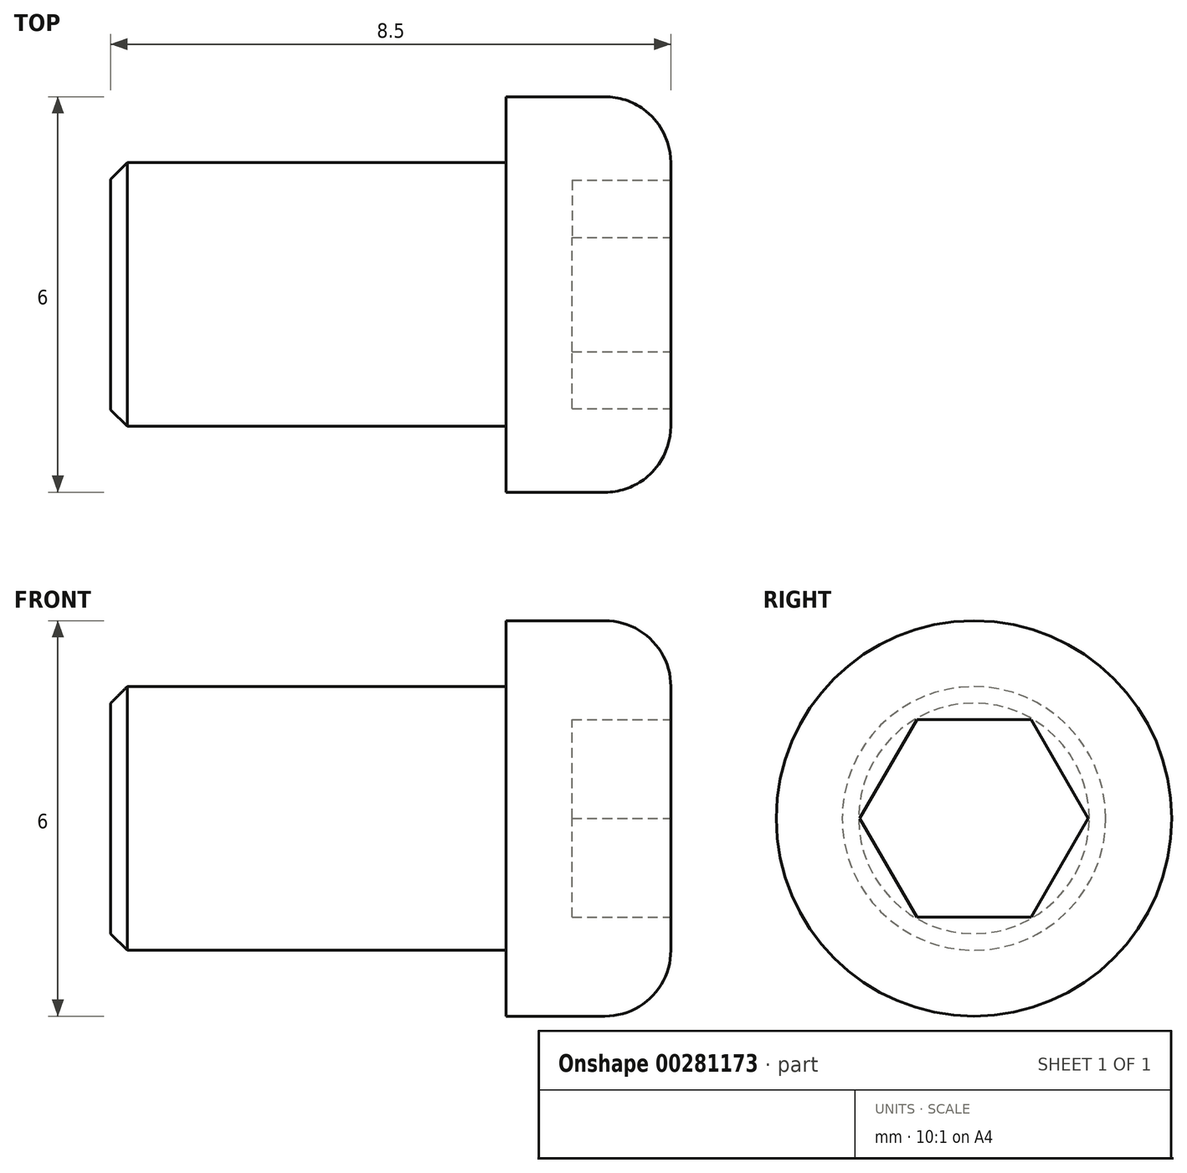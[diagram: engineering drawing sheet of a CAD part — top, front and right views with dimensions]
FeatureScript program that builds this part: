
annotation { "Feature Type Name" : "Feature", "Feature Type Description" : "" }
export const myFeature = defineFeature(function(context is Context, id is Id, definition is map)
    precondition{}
    {
        {
            var Q0;
            Q0=qCreatedBy(makeId("Front.planeOp"),FACE);
            var sketch = newSketch(context, id + "F0", { "sketchPlane" : qUnion([Q0])});
            skLineSegment(sketch, "E0", {"start": v(-4.25, 0) * mm, "end": v(-4.25, -2) * mm});
            skLineSegment(sketch, "E1", {"start": v(-4.25, -2) * mm, "end": v(1.75, -2) * mm});
            skLineSegment(sketch, "E2", {"start": v(1.75, -2) * mm, "end": v(1.75, -3) * mm});
            skLineSegment(sketch, "E3", {"start": v(1.75, -3) * mm, "end": v(4.25, -3) * mm});
            skLineSegment(sketch, "E4", {"start": v(4.25, -3) * mm, "end": v(4.25, 0) * mm});
            skLineSegment(sketch, "E5", {"start": v(4.25, 0) * mm, "end": v(-4.25, 0) * mm});
            skLineSegment(sketch, "E6", {"start": v(0, 0) * mm, "end": v(8.32, 0) * mm, "construction": true});
            skSolve(sketch);
        }
        {
            var Q0;
            Q0=makeQuery(id+"F0.imprint","IMPRINT",FACE,{"disambiguationData":[TD([[makeQuery(id+"F0.imprint","IMPRINT",EDGE,{"derivedFrom":sQuery(id+"F0.wireOp",EDGE,"E0")}),1.0]])]});
            var Q1;
            Q1=sQuery(id+"F0.wireOp",EDGE,"E6");
            revolve(context, id + "F1", {"entities" : qUnion([Q0]), "axis" : qUnion([Q1]), "revolveType" : RevolveType.FULL});
        }
        {
            var Q0;
            Q0=makeQuery(id+"F1.opRevolve","SWEPT_EDGE",EDGE,{"disambiguationData":[OSD([sQuery(id+"F0.wireOp",EDGE,"E0"),sQuery(id+"F0.wireOp",EDGE,"E1")])]});
            chamfer(context, id + "F2", {"entities" : qUnion([Q0]), "chamferType" : ChamferType.OFFSET_ANGLE, "width" : .25 * mm, "oppositeDirection" : false, "angle" : 45 * degree, "tangentPropagation" : true});
        }
        {
            var Q0;
            Q0=makeQuery(id+"F1.opRevolve","SWEPT_EDGE",EDGE,{"disambiguationData":[OSD([sQuery(id+"F0.wireOp",EDGE,"E3"),sQuery(id+"F0.wireOp",EDGE,"E4")])]});
            fillet(context, id + "F3", {"entities" : qUnion([Q0]), "radius" : 1 * mm, "tangentPropagation" : true, "allowEdgeOverflow" : false});
        }
        {
            var Q0;
            Q0=makeQuery(id+"F1.opRevolve","SWEPT_FACE",FACE,{"disambiguationData":[OSD([sQuery(id+"F0.wireOp",EDGE,"E4")])]});
            var sketch = newSketch(context, id + "F4", { "sketchPlane" : qUnion([Q0])});
            skPoint(sketch, "E7.0", {"position": v(0, 0) * mm});
            skCircle(sketch, "E8.cCircle", {"center": v(0, 0) * mm, "radius": 1.5 * mm, "construction": true});
            skLineSegment(sketch, "E8.0", {"start": v(-0.87, 1.5) * mm, "end": v(0.87, 1.5) * mm});
            skLineSegment(sketch, "E8.1", {"start": v(0.87, 1.5) * mm, "end": v(1.73, 0) * mm});
            skLineSegment(sketch, "E8.2", {"start": v(1.73, 0) * mm, "end": v(0.87, -1.5) * mm});
            skLineSegment(sketch, "E8.3", {"start": v(0.87, -1.5) * mm, "end": v(-0.87, -1.5) * mm});
            skLineSegment(sketch, "E8.4", {"start": v(-0.87, -1.5) * mm, "end": v(-1.73, 0) * mm});
            skLineSegment(sketch, "E8.5", {"start": v(-1.73, 0) * mm, "end": v(-0.87, 1.5) * mm});
            skPoint(sketch, "E8.0.midPoint", {"position": v(0, 1.5) * mm});
            skSolve(sketch);
        }
        {
            var Q0;
            Q0=qSketchRegion(id+"F4",true);
            extrude(context, id + "F5", {"entities" : qUnion([Q0]), "operationType" : NewBodyOperationType.REMOVE, "oppositeDirection" : true, "depth" : 1.5 * mm});
        }
    });
